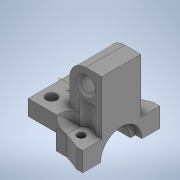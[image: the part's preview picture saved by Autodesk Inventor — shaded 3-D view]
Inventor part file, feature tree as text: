
AUTODESK INVENTOR PART (.ipt)
format: ipt  version: 2022 (Build 260153000, 153)  size: 377,856 bytes
history: native  units: mm
features: extrude x14, sketch x14, reference x11, projected_geometry x6, other x5, fillet x3, chamfer x2, plane x1
ambient origin geometry x8: Origin, YZ Plane, XZ Plane, XY Plane, X Axis, Y Axis, Z Axis, Center Point
bodies: Solid1 (feature_tree)
feature tree (56):
  extrude  "Extrusion1"  Depth=11.5mm
  extrude  "Extrusion2"  Depth=4.0mm TaperAngle=0.0deg
  extrude  "Extrusion3"  Depth=15.0mm
  extrude  "Extrusion4"  Depth=8.0mm
  extrude  "Extrusion5"  Depth=6.0mm TaperAngle=0.0deg
  extrude  "Extrusion6"  Depth=3.0mm
  extrude  "Extrusion7"  Depth=12.4mm
  sketch  "Sketch8"  dims[d23=6.2mm d24=6.2mm]
  extrude  "Extrusion8"  Depth=6.2mm
  extrude  "Extrusion9"  Depth=8.2mm
  fillet  "Fillet1"  Radius=4.0mm
  extrude  "Extrusion10"  Depth=6.2mm
  chamfer  "Chamfer1"  Distance=11.0mm
  extrude  "Extrusion12"  Depth=5.0mm
  fillet  "Fillet2"  Radius=5.0mm
  extrude  "Extrusion13"  Depth=8.0mm
  extrude  "Extrusion14"  Depth=5.0mm
  fillet  "Fillet3"  Radius=11.0mm
  plane  "Work Plane1"
  extrude  "Extrusion15"  Depth=3.9mm
  chamfer  "Chamfer3"  Distance=4.0mm
  sketch  "Sketch1"  dims[d0=11.5mm d1=0.0mm d2=12.1mm]
  reference  "Reference1"
  reference  "Reference2"
  sketch  "Sketch2"  dims[d3=11.5mm d4=0.0mm d5=4.0mm d6=0.0mm]
  sketch  "Sketch3"  dims[d7=2.4mm d8=0.0mm d9=15.0mm]
  reference  "Reference3"
  projected_geometry  "Projected Loop1"
  sketch  "Sketch4"  dims[d12=17.0mm d13=0.0mm d14=8.0mm]
  reference  "Reference4"
  projected_geometry  "Projected Loop2"
  sketch  "Sketch5"  dims[d15=8.0mm d16=6.0mm d17=0.0mm]
  projected_geometry  "Projected Loop3"
  sketch  "Sketch6"  dims[d18=3.0mm d19=3.0mm]
  sketch  "Sketch7"  dims[d20=5.5mm d21=12.4mm]
  sketch  "Sketch9"  dims[d25=27.25mm d26=0.0mm d27=8.2mm d28=4.0mm d29=0.0mm]
  projected_geometry  "Projected Loop4"
  projected_geometry  "Projected Loop5"
  projected_geometry  "Projected Loop6"
  sketch  "Sketch10"  dims[d30=4.0mm d31=0.0mm d32=6.2mm]
  reference  "Reference5"
  reference  "Reference6"
  sketch  "Sketch12"  dims[d33=6.0mm d34=11.0mm d35=0.0mm]
  reference  "Reference9"
  reference  "Reference10"
  sketch  "Sketch13"  dims[d40=1.0mm d41=2.0mm d42=45.0deg d48=5.0mm d49=5.0mm]
  reference  "Reference11"
  sketch  "Sketch14"  dims[d50=8.0mm d51=4.2mm]
  reference  "Reference12"
  reference  "Reference13"
  sketch  "Sketch15"  dims[d52=4.0mm d53=5.0mm d54=11.0mm d55=0.0mm d56=3.9mm d57=4.0mm d58=0.0mm d59=2.5mm d60=0.0mm d61=6.2mm d62=-12.5mm d64=2.0mm d66=2.0mm d67=2.5mm d68=2.0mm d69=1.0mm d70=6.0mm d71=4.0mm d72=0.0mm d73=2.0mm d75=0.0mm d76=0.5mm d77=2.0mm d78=45.0deg]
  other  "toolhead v2.iam"
  other  "Toolplate  V2:1"
  other  "E3D-VOLCANO-1.75-MO:1"
  other  "volcano tool.iam"
  other  "sherpa_mini_release1:1"
